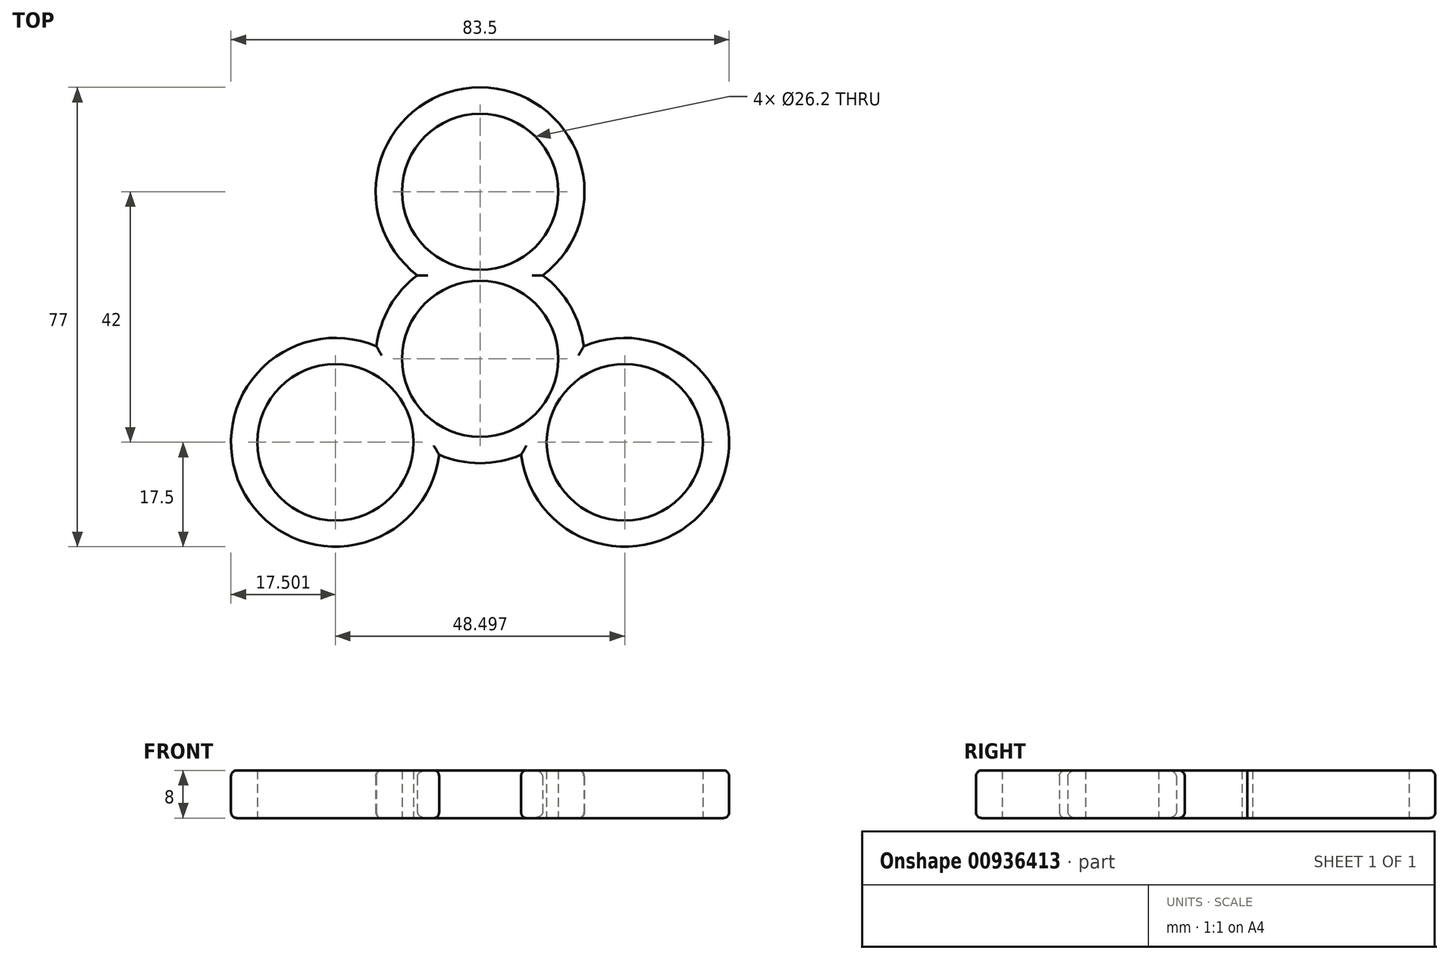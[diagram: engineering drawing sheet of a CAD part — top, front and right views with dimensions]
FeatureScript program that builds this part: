
annotation { "Feature Type Name" : "Feature", "Feature Type Description" : "" }
export const myFeature = defineFeature(function(context is Context, id is Id, definition is map)
    precondition{}
    {
        {
            var Q0;
            Q0=qCreatedBy(makeId("Top.planeOp"),FACE);
            var sketch = newSketch(context, id + "F0", { "sketchPlane" : qUnion([Q0])});
            skCircle(sketch, "E0", {"center": v(0, 0) * mm, "radius": 13.1 * mm});
            skCircle(sketch, "E1", {"center": v(-24.25, -14) * mm, "radius": 13.1 * mm});
            skCircle(sketch, "E2", {"center": v(24.25, -14) * mm, "radius": 13.1 * mm});
            skCircle(sketch, "E3", {"center": v(0, 28) * mm, "radius": 13.1 * mm});
            skLineSegment(sketch, "E4", {"start": v(0, 0) * mm, "end": v(-24.25, -14) * mm, "construction": true});
            skLineSegment(sketch, "E5", {"start": v(0, 0) * mm, "end": v(24.25, -14) * mm, "construction": true});
            skLineSegment(sketch, "E6", {"start": v(0, 0) * mm, "end": v(0, 28) * mm, "construction": true});
            skArc(sketch, "E7", {"start": v(-6.87, -16.1) * mm, "mid": v(0, -17.5) * mm, "end": v(6.87, -16.1) * mm});
            skArc(sketch, "E8", {"start": v(-17.37, 2.1) * mm, "mid": v(-39.4, -22.75) * mm, "end": v(-6.87, -16.1) * mm});
            skArc(sketch, "E9", {"start": v(6.87, -16.1) * mm, "mid": v(39.4, -22.75) * mm, "end": v(17.37, 2.1) * mm});
            skArc(sketch, "E10", {"start": v(10.5, 14) * mm, "mid": v(0, 45.5) * mm, "end": v(-10.5, 14) * mm});
            skArc(sketch, "E11.trimOffspring", {"start": v(-10.5, 14) * mm, "mid": v(-15.16, 8.75) * mm, "end": v(-17.37, 2.1) * mm});
            skArc(sketch, "E12.trimOffspring", {"start": v(17.37, 2.1) * mm, "mid": v(15.16, 8.75) * mm, "end": v(10.5, 14) * mm});
            skSolve(sketch);
        }
        {
            var Q0;
            Q0 = qSketchRegion(id + "F0", true);
            extrude(context, id + "F1", {"entities" : qUnion([Q0]), "depth" : 8 * mm, "offsetDistance" : 25 * mm});
        }
        {
            var Q0;
            Q0=makeQuery(id+"F1.opExtrude","CAP_EDGE",EDGE,{"disambiguationData":[OSD([sQuery(id+"F0.wireOp",EDGE,"E8")])],"isStart":false});
            var Q1;
            Q1=makeQuery(id+"F1.opExtrude","CAP_EDGE",EDGE,{"disambiguationData":[OSD([sQuery(id+"F0.wireOp",EDGE,"E11.trimOffspring")])],"isStart":false});
            var Q2;
            Q2=makeQuery(id+"F1.opExtrude","CAP_EDGE",EDGE,{"disambiguationData":[OSD([sQuery(id+"F0.wireOp",EDGE,"E10")])],"isStart":false});
            var Q3;
            Q3=makeQuery(id+"F1.opExtrude","CAP_EDGE",EDGE,{"disambiguationData":[OSD([sQuery(id+"F0.wireOp",EDGE,"E12.trimOffspring")])],"isStart":false});
            var Q4;
            Q4=makeQuery(id+"F1.opExtrude","CAP_EDGE",EDGE,{"disambiguationData":[OSD([sQuery(id+"F0.wireOp",EDGE,"E9")])],"isStart":false});
            var Q5;
            Q5=makeQuery(id+"F1.opExtrude","CAP_EDGE",EDGE,{"disambiguationData":[OSD([sQuery(id+"F0.wireOp",EDGE,"E7")])],"isStart":false});
            var Q6;
            Q6=makeQuery(id+"F1.opExtrude","CAP_EDGE",EDGE,{"disambiguationData":[OSD([sQuery(id+"F0.wireOp",EDGE,"E8")])],"isStart":true});
            var Q7;
            Q7=makeQuery(id+"F1.opExtrude","CAP_EDGE",EDGE,{"disambiguationData":[OSD([sQuery(id+"F0.wireOp",EDGE,"E7")])],"isStart":true});
            var Q8;
            Q8=makeQuery(id+"F1.opExtrude","CAP_EDGE",EDGE,{"disambiguationData":[OSD([sQuery(id+"F0.wireOp",EDGE,"E9")])],"isStart":true});
            var Q9;
            Q9=makeQuery(id+"F1.opExtrude","CAP_EDGE",EDGE,{"disambiguationData":[OSD([sQuery(id+"F0.wireOp",EDGE,"E12.trimOffspring")])],"isStart":true});
            var Q10;
            Q10=makeQuery(id+"F1.opExtrude","CAP_EDGE",EDGE,{"disambiguationData":[OSD([sQuery(id+"F0.wireOp",EDGE,"E10")])],"isStart":true});
            var Q11;
            Q11=makeQuery(id+"F1.opExtrude","CAP_EDGE",EDGE,{"disambiguationData":[OSD([sQuery(id+"F0.wireOp",EDGE,"E11.trimOffspring")])],"isStart":true});
            fillet(context, id + "F2", {"entities" : qUnion([Q0, Q1, Q2, Q3, Q4, Q5, Q6, Q7, Q8, Q9, Q10, Q11]), "radius" : 1 * mm, "tangentPropagation" : true, "allowEdgeOverflow" : false});
        }
    });
